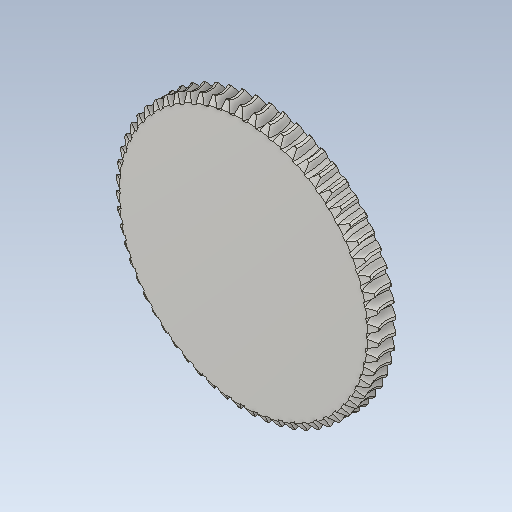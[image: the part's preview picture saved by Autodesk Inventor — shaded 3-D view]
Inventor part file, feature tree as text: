
AUTODESK INVENTOR PART (.ipt)
format: ipt  version: 2021.1 (Build 251245010, 245A)  size: 1,144,832 bytes
history: native  units: mm (DEFAULTED — no unit token found)
features: other x8, plane x3, pattern_circular x1, sketch x1
ambient origin geometry x5: Origin, X Axis, Y Axis, Z Axis, Center Point
bodies: Solid1 (feature_tree)
feature tree (13):
  other  "Tooth Plane"
  other  "Base Body Sketch"
  other  "Base Body"
  other  "Base Body2"
  plane  "Work Plane13"
  other  "Tooth"
  pattern_circular  "Tooth Pattern"  [2 undecoded]
  plane  "Work Plane14"
  plane  "Work Plane15"
  other  "Tooth Sketch"
  sketch  "Sketch8"  dims[d35=90.0deg d37=-0.996687mm d38=70.744372mm d39=3.490659mm d40=7.680818mm d41=10.106339mm d42=1.905mm d43=90.0deg d44=600.0mm d46=360.0deg d50=5.318254mm d68=70.744372mm d69=0.0mm d73=0.0mm d75=0.523599mm d77=121.276067mm d78=12.3mm d79=0.0mm d80=0.0mm d81=0.0mm d82=0.0mm d83=0.523599mm d84=0.0mm d85=180.0deg d86=70.744372mm d87=127.33987mm d89=16.170142mm d90=90.0deg d92=12.3mm d93=70.744372mm]
  other  "Srf1"
  other  "Pitch Diameter"
note: 2 required parameter values undecoded (feature->parameter linkage not recoverable at this tier; creation-order binding heuristic only, values carry confidence <= 0.55)
